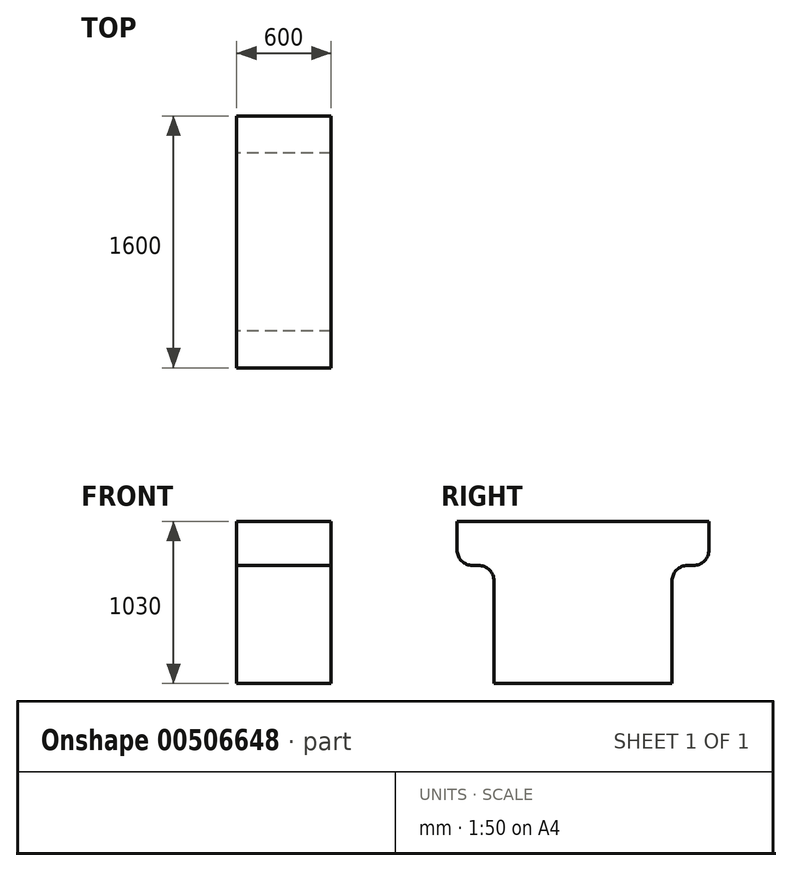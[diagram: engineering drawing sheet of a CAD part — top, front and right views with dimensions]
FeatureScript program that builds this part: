
annotation { "Feature Type Name" : "Feature", "Feature Type Description" : "" }
export const myFeature = defineFeature(function(context is Context, id is Id, definition is map)
    precondition{}
    {
        {
            var Q0;
            Q0=qCreatedBy(makeId("Right.planeOp"),FACE);
            var sketch = newSketch(context, id + "F0", { "sketchPlane" : qUnion([Q0])});
            skLineSegment(sketch, "E0.bottom", {"start": v(234.74, 0) * mm, "end": v(1365.26, 0) * mm});
            skLineSegment(sketch, "E0.top", {"start": v(0, 1030) * mm, "end": v(1600, 1030) * mm});
            skLineSegment(sketch, "E0.left", {"start": v(0, 750) * mm, "end": v(0, 1030) * mm});
            skLineSegment(sketch, "E0.right", {"start": v(1600, 750) * mm, "end": v(1600, 1030) * mm});
            skLineSegment(sketch, "E1", {"start": v(800, 0) * mm, "end": v(800, 788.08) * mm, "construction": true});
            skPoint(sketch, "E1.endSnap0", {"position": v(800, 0) * mm});
            skLineSegment(sketch, "E2", {"start": v(234.74, 0) * mm, "end": v(234.74, 750) * mm});
            skLineSegment(sketch, "E3", {"start": v(234.74, 750) * mm, "end": v(0, 750) * mm});
            skLineSegment(sketch, "E4.MirrorCS", {"start": v(1365.26, 0) * mm, "end": v(1365.26, 750) * mm});
            skLineSegment(sketch, "E5.MirrorCS", {"start": v(1365.26, 750) * mm, "end": v(1600, 750) * mm});
            skPoint(sketch, "E6.orphan", {"position": v(0, 0) * mm});
            skPoint(sketch, "E7.orphan", {"position": v(1600, 0) * mm});
            skSolve(sketch);
        }
        {
            var Q0;
            Q0 = qSketchRegion(id + "F0", true);
            extrude(context, id + "F1", {"entities" : qUnion([Q0]), "depth" : 600 * mm});
        }
        {
            var Q0;
            Q0=makeQuery(id+"F1.opExtrude","SWEPT_EDGE",EDGE,{"disambiguationData":[OSD([sQuery(id+"F0.wireOp",EDGE,"E2"),sQuery(id+"F0.wireOp",EDGE,"E3")])]});
            var Q1;
            Q1=makeQuery(id+"F1.opExtrude","SWEPT_EDGE",EDGE,{"disambiguationData":[OSD([sQuery(id+"F0.wireOp",EDGE,"E0.left"),sQuery(id+"F0.wireOp",EDGE,"E3")])]});
            var Q2;
            Q2=makeQuery(id+"F1.opExtrude","SWEPT_EDGE",EDGE,{"disambiguationData":[OSD([sQuery(id+"F0.wireOp",EDGE,"E4.MirrorCS"),sQuery(id+"F0.wireOp",EDGE,"E5.MirrorCS")])]});
            var Q3;
            Q3=makeQuery(id+"F1.opExtrude","SWEPT_EDGE",EDGE,{"disambiguationData":[OSD([sQuery(id+"F0.wireOp",EDGE,"E0.right"),sQuery(id+"F0.wireOp",EDGE,"E5.MirrorCS")])]});
            fillet(context, id + "F2", {"entities" : qUnion([Q0, Q1, Q2, Q3]), "radius" : 100 * mm, "tangentPropagation" : true, "allowEdgeOverflow" : false});
        }
    });
